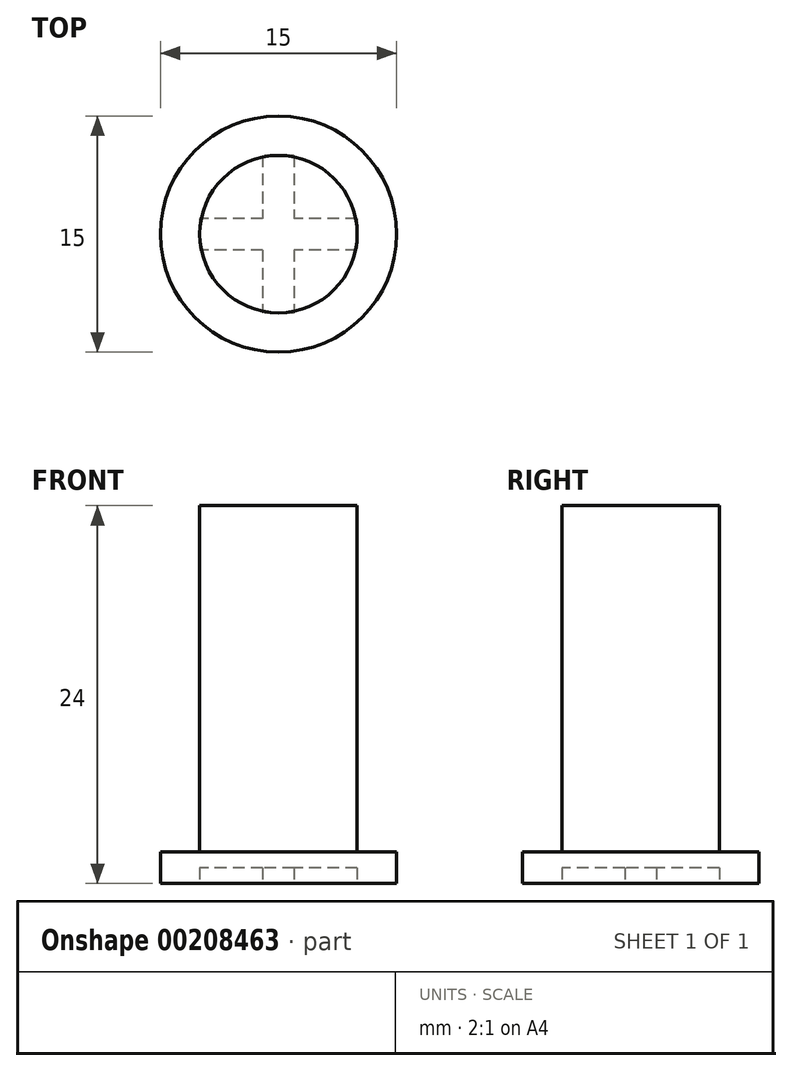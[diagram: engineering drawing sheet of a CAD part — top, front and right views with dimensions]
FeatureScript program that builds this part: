
annotation { "Feature Type Name" : "Feature", "Feature Type Description" : "" }
export const myFeature = defineFeature(function(context is Context, id is Id, definition is map)
    precondition{}
    {
        {
            var Q0;
            Q0=qCreatedBy(makeId("Top.planeOp"),FACE);
            var sketch = newSketch(context, id + "F0", { "sketchPlane" : qUnion([Q0])});
            skCircle(sketch, "E0", {"center": v(0, 0) * mm, "radius": 7.5 * mm});
            skSolve(sketch);
        }
        {
            var Q0;
            Q0=makeQuery(id+"F0.imprint","IMPRINT",FACE,{"disambiguationData":[TD([[makeQuery(id+"F0.imprint","IMPRINT",EDGE,{"derivedFrom":sQuery(id+"F0.wireOp",EDGE,"E0")}),1.0]])]});
            extrude(context, id + "F1", {"entities" : qUnion([Q0]), "depth" : 2 * mm});
        }
        {
            var Q0;
            Q0=makeQuery(id+"F1.opExtrude","CAP_FACE",FACE,{"disambiguationData":[OSD([sQuery(id+"F0.wireOp",EDGE,"E0")])],"isStart":false});
            var sketch = newSketch(context, id + "F2", { "sketchPlane" : qUnion([Q0])});
            skCircle(sketch, "E1", {"center": v(0, 0) * mm, "radius": 5 * mm});
            skSolve(sketch);
        }
        {
            var Q0;
            Q0=qSketchRegion(id+"F2",true);
            extrude(context, id + "F3", {"entities" : qUnion([Q0]), "operationType" : NewBodyOperationType.ADD, "depth" : 22 * mm});
        }
        {
            var Q0;
            Q0=makeQuery(id+"F1.opExtrude","CAP_FACE",FACE,{"disambiguationData":[OSD([sQuery(id+"F0.wireOp",EDGE,"E0")])],"isStart":true});
            var sketch = newSketch(context, id + "F4", { "sketchPlane" : qUnion([Q0])});
            skLineSegment(sketch, "E2.bottom", {"start": v(5, -1) * mm, "end": v(-5, -1) * mm});
            skLineSegment(sketch, "E2.top", {"start": v(5, 1) * mm, "end": v(-5, 1) * mm});
            skLineSegment(sketch, "E2.left", {"start": v(5, -1) * mm, "end": v(5, 1) * mm});
            skLineSegment(sketch, "E2.right", {"start": v(-5, -1) * mm, "end": v(-5, 1) * mm});
            skPoint(sketch, "E2.middle", {"position": v(0, 0) * mm});
            skLineSegment(sketch, "E3.bottom", {"start": v(1, -5) * mm, "end": v(-1, -5) * mm});
            skLineSegment(sketch, "E3.top", {"start": v(1, 5) * mm, "end": v(-1, 5) * mm});
            skLineSegment(sketch, "E3.left", {"start": v(1, -5) * mm, "end": v(1, 5) * mm});
            skLineSegment(sketch, "E3.right", {"start": v(-1, -5) * mm, "end": v(-1, 5) * mm});
            skSolve(sketch);
        }
        {
            var Q0;
            Q0=qSketchRegion(id+"F4",true);
            extrude(context, id + "F5", {"entities" : qUnion([Q0]), "operationType" : NewBodyOperationType.REMOVE, "oppositeDirection" : true, "depth" : 1 * mm});
        }
    });
